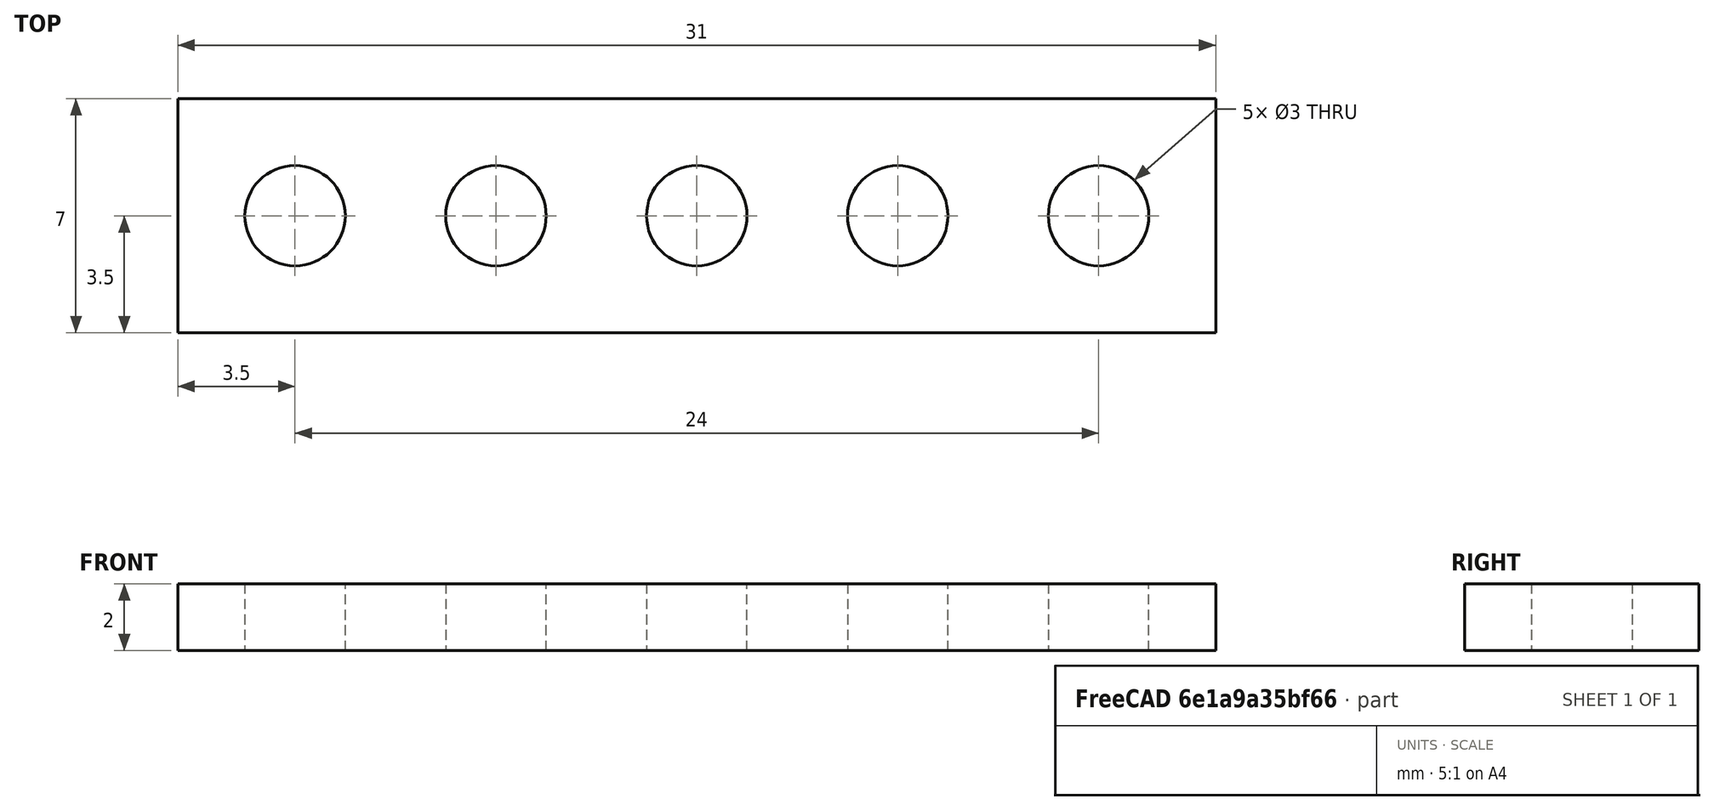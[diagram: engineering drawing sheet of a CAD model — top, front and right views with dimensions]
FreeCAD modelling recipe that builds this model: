
FCSTD DOCUMENT  (FreeCAD 1.0R39319 (Git))
Label: ojt1_t10r01_array_cylinder
License: All rights reserved
LicenseURL: https://en.wikipedia.org/wiki/All_rights_reserved
objects: Part::Box×1, Part::Cylinder×1, Part::FeaturePython×1, Part::Cut×1
note: 3 computed .brp shape members not serialized (recipe doc carries the construction recipe); baked Part::Feature solids carry a one-line shape summary decoded from their .brp

FEATURE [Part::Box] Box  label="Cube"
  AttacherType = Attacher::AttachEngine3D
  Height = 2
  Length = 31
  Width = 7
FEATURE [Part::Cylinder] Cylinder
  Angle = 360
  AttacherType = Attacher::AttachEngine3D
  FirstAngle = 0
  Height = 2
  Placement = pos=(3.5,3.5,0) rot=(0,0,1;0rad)
  Radius = 1.5
  SecondAngle = 0
FEATURE [Part::FeaturePython] Array  # Draft array (typed FeaturePython)
  AlwaysSyncPlacement = false
  Angle = 360
  ArrayType = 0
  Axis = (0,0,1)
  Base = -> Cylinder
  Center = (-6.07,11.08,0)
  Count = 5
  ExpandArray = false
  Fuse = false
  IntervalAxis = (0,0,0)
  IntervalX = (6,0,0)
  IntervalY = (0,0,0)
  IntervalZ = (0,0,50)
  NumberCircles = 3
  NumberPolar = 5
  NumberX = 5
  NumberY = 0
  NumberZ = 1
  PlacementList = 5 placements: arithmetic series from (3.5,3.5,0) step (6,0,0) to (27.5,3.5,0)
  RadialDistance = 50
  ScaleList = (5) [(1,1,1),(1,1,1),(1,1,1),(1,1,1),(1,1,1)]
  Symmetry = 1
  TangentialDistance = 25
FEATURE [Part::Cut] Cut
  Base = -> Box
  Refine = true
  Tool = -> Array
